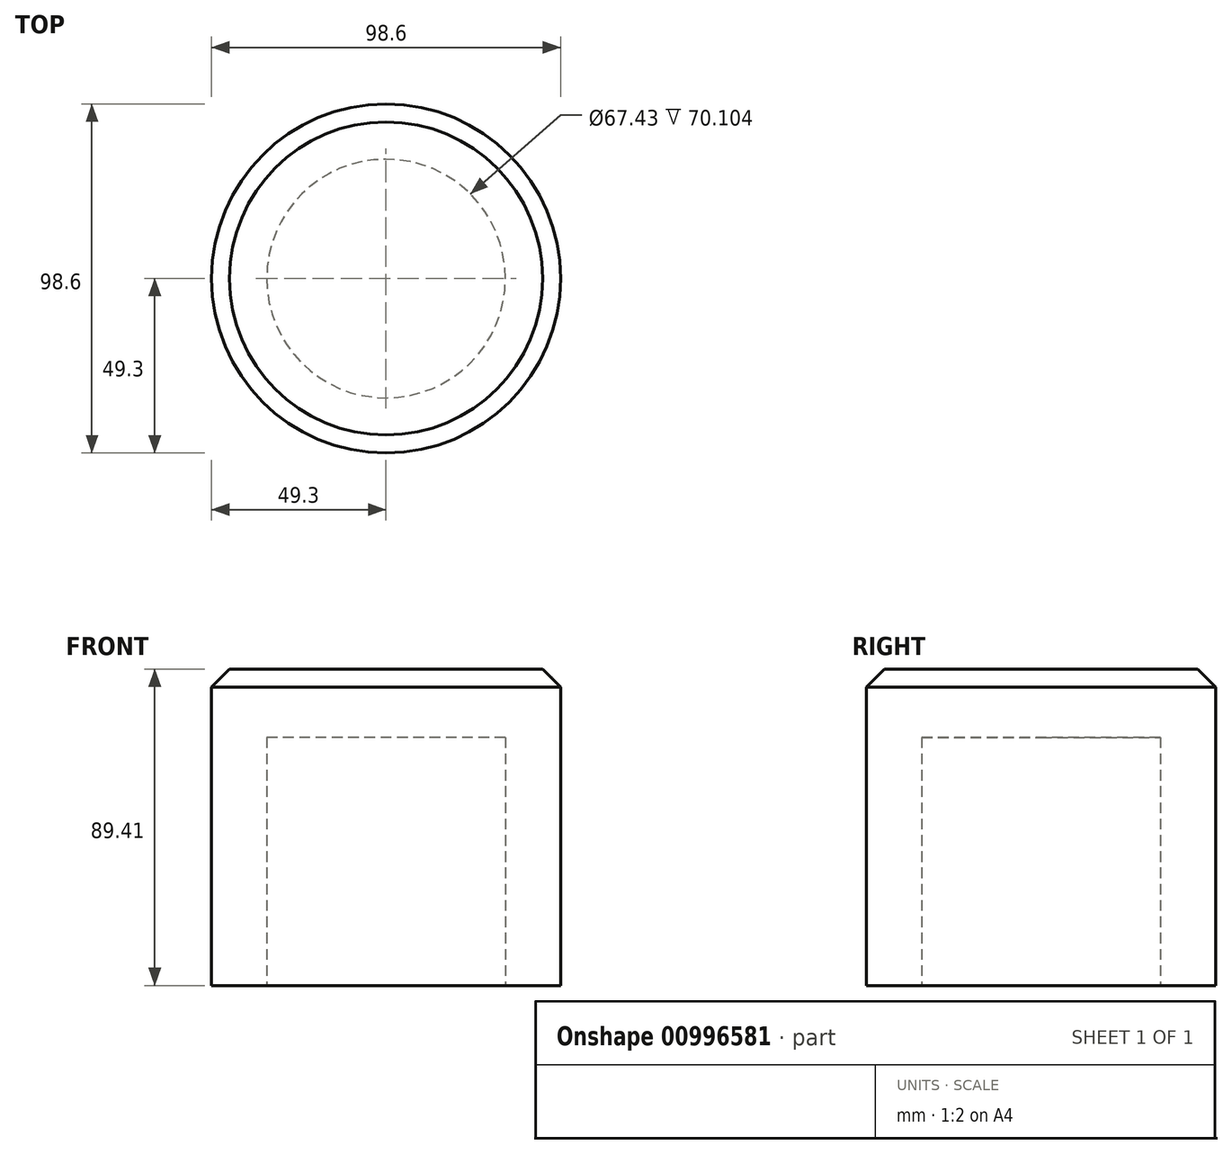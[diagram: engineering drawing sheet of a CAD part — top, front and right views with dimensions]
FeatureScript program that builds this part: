
annotation { "Feature Type Name" : "Feature", "Feature Type Description" : "" }
export const myFeature = defineFeature(function(context is Context, id is Id, definition is map)
    precondition{}
    {
        {
            var Q0;
            Q0=qCreatedBy(makeId("Top.planeOp"),FACE);
            var sketch = newSketch(context, id + "F0", { "sketchPlane" : qUnion([Q0])});
            skCircle(sketch, "E0", {"center": v(0, 0) * mm, "radius": 49.3 * mm});
            skSolve(sketch);
        }
        {
            var Q0;
            Q0=makeQuery(id+"F0.imprint","IMPRINT",FACE,{"disambiguationData":[TD([[makeQuery(id+"F0.imprint","IMPRINT",EDGE,{"derivedFrom":sQuery(id+"F0.wireOp",EDGE,"E0")}),1.0]])]});
            extrude(context, id + "F1", {"entities" : qUnion([Q0]), "depth" : 89.4 * mm, "offsetDistance" : 25.4 * mm});
        }
        {
            var Q0;
            Q0=makeQuery(id+"F1.opExtrude","CAP_FACE",FACE,{"disambiguationData":[OSD([sQuery(id+"F0.wireOp",EDGE,"E0")])],"isStart":false});
            chamfer(context, id + "F2", {"entities" : qUnion([Q0]), "width" : 5.08 * mm, "tangentPropagation" : true});
        }
        {
            var Q0;
            Q0=qCreatedBy(makeId("Top.planeOp"),FACE);
            var sketch = newSketch(context, id + "F3", { "sketchPlane" : qUnion([Q0])});
            skCircle(sketch, "E1", {"center": v(0, 0) * mm, "radius": 33.71 * mm});
            skSolve(sketch);
        }
        {
            var Q0;
            Q0 = qSketchRegion(id + "F3", true);
            extrude(context, id + "F4", {"entities" : qUnion([Q0]), "operationType" : NewBodyOperationType.REMOVE, "depth" : 70.1 * mm, "offsetDistance" : 25.4 * mm});
        }
    });
